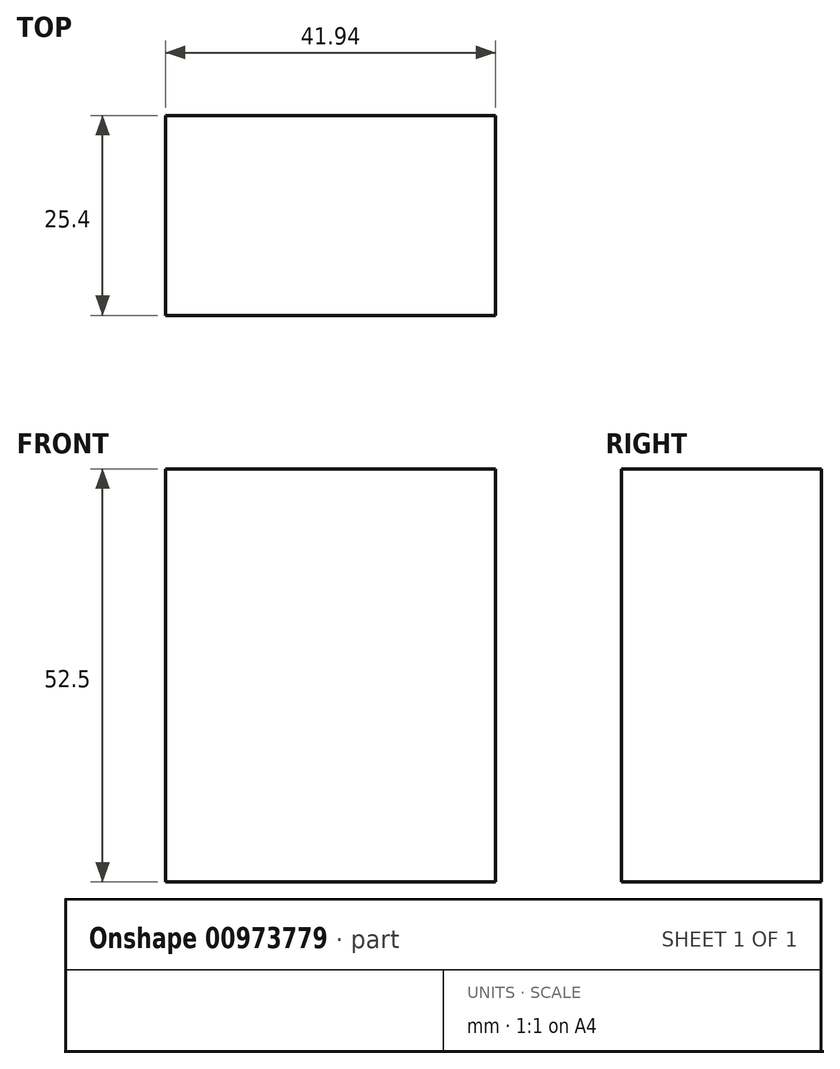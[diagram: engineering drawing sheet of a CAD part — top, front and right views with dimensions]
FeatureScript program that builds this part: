
annotation { "Feature Type Name" : "Feature", "Feature Type Description" : "" }
export const myFeature = defineFeature(function(context is Context, id is Id, definition is map)
    precondition{}
    {
        {
            var Q0;
            Q0=qCreatedBy(makeId("Front.planeOp"),FACE);
            var sketch = newSketch(context, id + "F0", { "sketchPlane" : qUnion([Q0])});
            skLineSegment(sketch, "E0.bottom", {"start": v(21.42, 35.6) * mm, "end": v(-20.52, 35.6) * mm});
            skLineSegment(sketch, "E0.top", {"start": v(21.42, -16.9) * mm, "end": v(-20.52, -16.9) * mm});
            skLineSegment(sketch, "E0.left", {"start": v(21.42, 35.6) * mm, "end": v(21.42, -16.9) * mm});
            skLineSegment(sketch, "E0.right", {"start": v(-20.52, 35.6) * mm, "end": v(-20.52, -16.9) * mm});
            skSolve(sketch);
        }
        {
            var Q0;
            Q0 = qSketchRegion(id + "F0", true);
            extrude(context, id + "F1", {"entities" : qUnion([Q0]), "depth" : 25.4 * mm, "offsetDistance" : 25.4 * mm});
        }
    });
